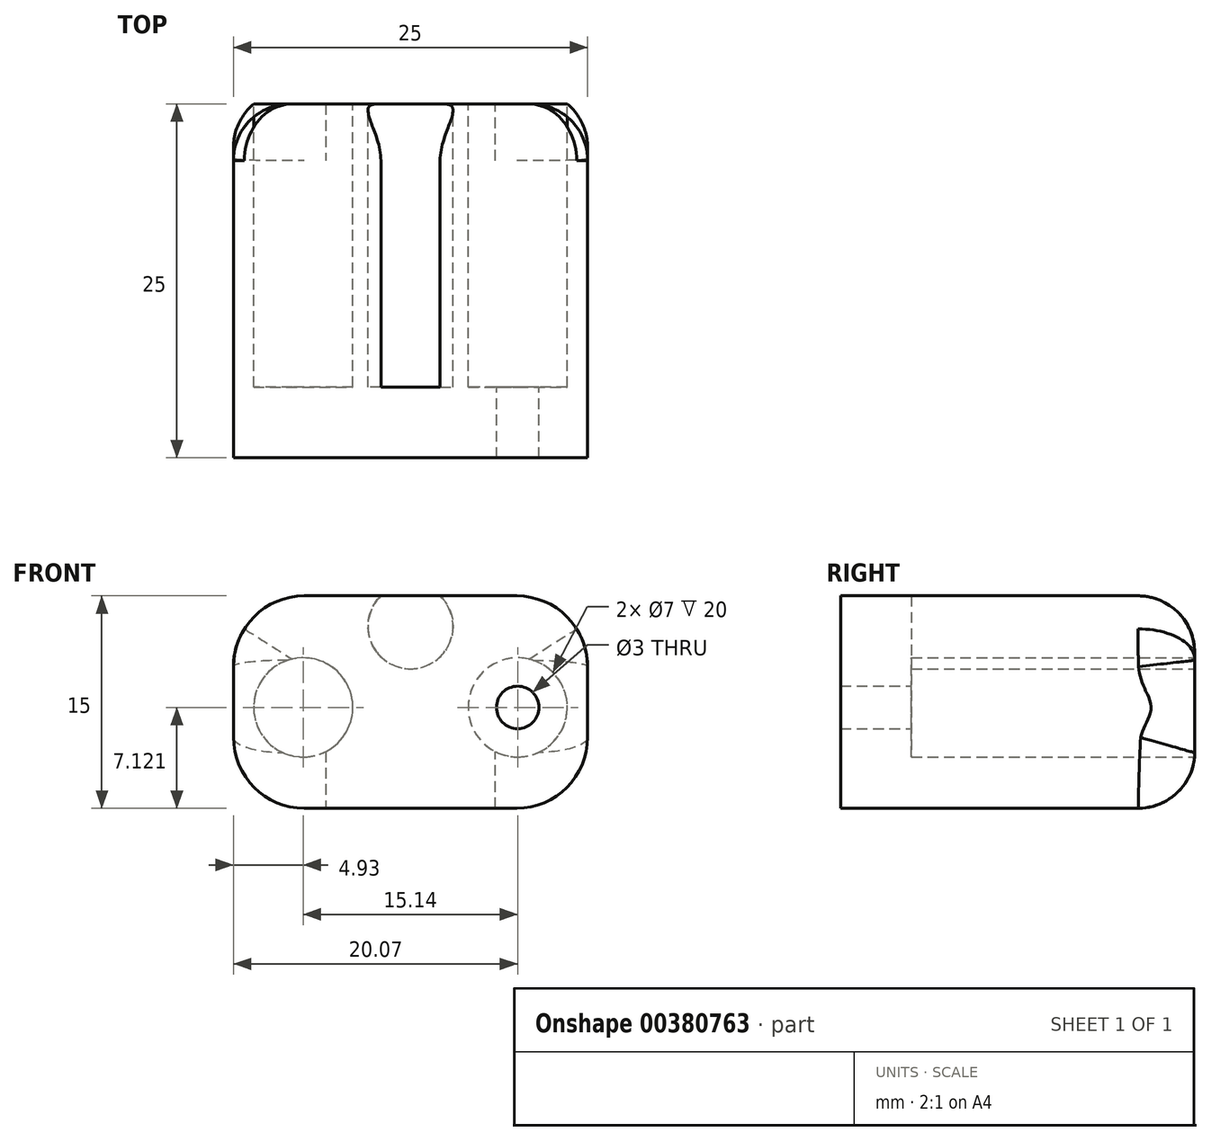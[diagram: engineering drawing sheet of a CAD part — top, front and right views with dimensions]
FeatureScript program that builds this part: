
annotation { "Feature Type Name" : "Feature", "Feature Type Description" : "" }
export const myFeature = defineFeature(function(context is Context, id is Id, definition is map)
    precondition{}
    {
        {
            var Q0;
            Q0=qCreatedBy(makeId("Front.planeOp"),FACE);
            var sketch = newSketch(context, id + "F0", { "sketchPlane" : qUnion([Q0])});
            skLineSegment(sketch, "E0.bottom", {"start": v(-12.5, 0) * mm, "end": v(12.5, 0) * mm});
            skLineSegment(sketch, "E0.top", {"start": v(-12.5, -15) * mm, "end": v(12.5, -15) * mm});
            skLineSegment(sketch, "E0.left", {"start": v(-12.5, 0) * mm, "end": v(-12.5, -15) * mm});
            skLineSegment(sketch, "E0.right", {"start": v(12.5, 0) * mm, "end": v(12.5, -15) * mm});
            skSolve(sketch);
        }
        {
            var Q0;
            Q0 = qSketchRegion(id + "F0", true);
            extrude(context, id + "F1", {"entities" : qUnion([Q0]), "depth" : 25 * mm});
        }
        {
            var Q0;
            Q0=qCreatedBy(makeId("Front.planeOp"),FACE);
            var sketch = newSketch(context, id + "F2", { "sketchPlane" : qUnion([Q0])});
            skCircle(sketch, "E1", {"center": v(0, -2.15) * mm, "radius": 3 * mm});
            skSolve(sketch);
        }
        {
            var Q0;
            Q0 = qSketchRegion(id + "F2", true);
            extrude(context, id + "F3", {"entities" : qUnion([Q0]), "operationType" : NewBodyOperationType.REMOVE, "depth" : 20 * mm});
        }
        {
            var Q0;
            Q0=qCreatedBy(makeId("Front.planeOp"),FACE);
            var sketch = newSketch(context, id + "F4", { "sketchPlane" : qUnion([Q0])});
            skCircle(sketch, "E2", {"center": v(7.57, -7.88) * mm, "radius": 1.5 * mm});
            skCircle(sketch, "E3.MirrorC", {"center": v(-7.57, -7.88) * mm, "radius": 1.5 * mm});
            skSolve(sketch);
        }
        {
            var Q0;
            Q0=makeQuery(id+"F4.imprint","IMPRINT",FACE,{"disambiguationData":[TD([[makeQuery(id+"F4.imprint","IMPRINT",EDGE,{"derivedFrom":sQuery(id+"F4.wireOp",EDGE,"E2")}),1.0]])]});
            var Q1;
            Q1=makeQuery(id+"F4.imprint","IMPRINT",FACE,{"disambiguationData":[TD([[makeQuery(id+"F4.imprint","IMPRINT",EDGE,{"derivedFrom":sQuery(id+"F4.wireOp",EDGE,"E3.MirrorC")}),-1.0]])]});
            extrude(context, id + "F5", {"entities" : qUnion([Q0, Q1]), "operationType" : NewBodyOperationType.REMOVE, "endBound" : BoundingType.SYMMETRIC, "depth" : 100 * mm});
        }
        {
            var Q0;
            Q0=qCreatedBy(makeId("Front.planeOp"),FACE);
            var sketch = newSketch(context, id + "F6", { "sketchPlane" : qUnion([Q0])});
            skCircle(sketch, "E4.0", {"center": v(7.57, -7.88) * mm, "radius": 3.5 * mm});
            skCircle(sketch, "E5.0", {"center": v(-7.57, -7.88) * mm, "radius": 3.5 * mm});
            skSolve(sketch);
        }
        {
            var Q0;
            Q0=makeQuery(id+"F6.imprint","IMPRINT",FACE,{"disambiguationData":[TD([[makeQuery(id+"F6.imprint","IMPRINT",EDGE,{"derivedFrom":sQuery(id+"F6.wireOp",EDGE,"E5.0")}),1.0]])]});
            var Q1;
            Q1=makeQuery(id+"F6.imprint","IMPRINT",FACE,{"disambiguationData":[TD([[makeQuery(id+"F6.imprint","IMPRINT",EDGE,{"derivedFrom":sQuery(id+"F6.wireOp",EDGE,"E4.0")}),1.0]])]});
            extrude(context, id + "F7", {"entities" : qUnion([Q0, Q1]), "operationType" : NewBodyOperationType.REMOVE, "depth" : 20 * mm});
        }
        {
            var Q0;
            Q0=makeQuery(id+"F1.opExtrude","SWEPT_EDGE",EDGE,{"disambiguationData":[OSD([sQuery(id+"F0.wireOp",EDGE,"E0.bottom"),sQuery(id+"F0.wireOp",EDGE,"E0.right")])]});
            var Q1;
            Q1=makeQuery(id+"F1.opExtrude","SWEPT_EDGE",EDGE,{"disambiguationData":[OSD([sQuery(id+"F0.wireOp",EDGE,"E0.top"),sQuery(id+"F0.wireOp",EDGE,"E0.right")])]});
            var Q2;
            Q2=makeQuery(id+"F1.opExtrude","SWEPT_EDGE",EDGE,{"disambiguationData":[OSD([sQuery(id+"F0.wireOp",EDGE,"E0.top"),sQuery(id+"F0.wireOp",EDGE,"E0.left")])]});
            var Q3;
            Q3=makeQuery(id+"F1.opExtrude","SWEPT_EDGE",EDGE,{"disambiguationData":[OSD([sQuery(id+"F0.wireOp",EDGE,"E0.bottom"),sQuery(id+"F0.wireOp",EDGE,"E0.left")])]});
            fillet(context, id + "F8", {"entities" : qUnion([Q0, Q1, Q2, Q3]), "radius" : 5 * mm, "tangentPropagation" : true, "allowEdgeOverflow" : false});
        }
        {
            var Q0;
            Q0=makeQuery(id+"F1.opExtrude","CAP_EDGE",EDGE,{"disambiguationData":[OSD([sQuery(id+"F0.wireOp",EDGE,"E0.right")])],"isStart":true});
            fillet(context, id + "F9", {"entities" : qUnion([Q0]), "radius" : 4 * mm, "tangentPropagation" : true, "allowEdgeOverflow" : false});
        }
    });
